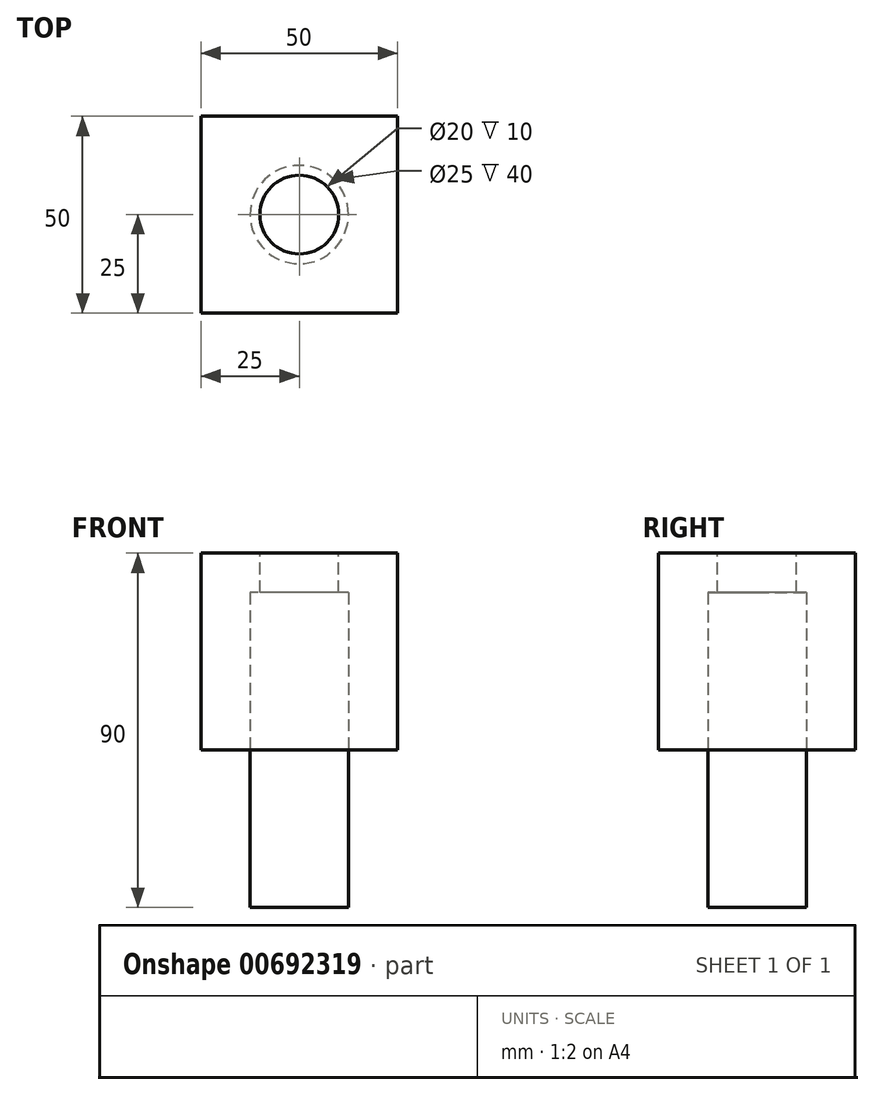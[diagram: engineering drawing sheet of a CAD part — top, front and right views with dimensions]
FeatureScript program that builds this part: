
annotation { "Feature Type Name" : "Feature", "Feature Type Description" : "" }
export const myFeature = defineFeature(function(context is Context, id is Id, definition is map)
    precondition{}
    {
        {
            var Q0;
            Q0=qCreatedBy(makeId("Top.planeOp"),FACE);
            var sketch = newSketch(context, id + "F0", { "sketchPlane" : qUnion([Q0])});
            skLineSegment(sketch, "E0.bottom", {"start": v(25, -25) * mm, "end": v(-25, -25) * mm});
            skLineSegment(sketch, "E0.top", {"start": v(25, 25) * mm, "end": v(-25, 25) * mm});
            skLineSegment(sketch, "E0.left", {"start": v(25, -25) * mm, "end": v(25, 25) * mm});
            skLineSegment(sketch, "E0.right", {"start": v(-25, -25) * mm, "end": v(-25, 25) * mm});
            skPoint(sketch, "E0.middle", {"position": v(0, 0) * mm});
            skSolve(sketch);
        }
        {
            var Q0;
            Q0=makeQuery(id+"F0.imprint","IMPRINT",FACE,{"disambiguationData":[TD([[makeQuery(id+"F0.imprint","IMPRINT",EDGE,{"derivedFrom":sQuery(id+"F0.wireOp",EDGE,"E0.bottom")}),-1.0]])]});
            extrude(context, id + "F1", {"entities" : qUnion([Q0]), "depth" : 50 * mm, "offsetDistance" : 25 * mm});
        }
        {
            var Q0;
            Q0=makeQuery(id+"F1.opExtrude","CAP_FACE",FACE,{"disambiguationData":[OSD([sQuery(id+"F0.wireOp",EDGE,"E0.bottom"),sQuery(id+"F0.wireOp",EDGE,"E0.top"),sQuery(id+"F0.wireOp",EDGE,"E0.left"),sQuery(id+"F0.wireOp",EDGE,"E0.right")])],"isStart":false});
            var sketch = newSketch(context, id + "F2", { "sketchPlane" : qUnion([Q0])});
            skCircle(sketch, "E1", {"center": v(0, 0) * mm, "radius": 10 * mm});
            skSolve(sketch);
        }
        {
            var Q0;
            Q0=makeQuery(id+"F2.imprint","IMPRINT",FACE,{"disambiguationData":[TD([[makeQuery(id+"F2.imprint","IMPRINT",EDGE,{"derivedFrom":sQuery(id+"F2.wireOp",EDGE,"E1")}),1.0]])]});
            extrude(context, id + "F3", {"entities" : qUnion([Q0]), "operationType" : NewBodyOperationType.REMOVE, "oppositeDirection" : true, "depth" : 25 * mm, "offsetDistance" : 25 * mm});
        }
        {
            var Q0;
            Q0=qCreatedBy(makeId("Top.planeOp"),FACE);
            var sketch = newSketch(context, id + "F4", { "sketchPlane" : qUnion([Q0])});
            skCircle(sketch, "E2", {"center": v(0, 0) * mm, "radius": 12.5 * mm});
            skSolve(sketch);
        }
        {
            var Q0;
            Q0=makeQuery(id+"F4.imprint","IMPRINT",FACE,{"disambiguationData":[TD([[makeQuery(id+"F4.imprint","IMPRINT",EDGE,{"derivedFrom":sQuery(id+"F4.wireOp",EDGE,"E2")}),1.0]])]});
            extrude(context, id + "F5", {"entities" : qUnion([Q0]), "endBound" : BoundingType.SYMMETRIC, "depth" : 80 * mm, "offsetDistance" : 25 * mm});
        }
        {
            var Q0;
            Q0=makeQuery(id+"F5.opExtrude","SWEPT_BODY",BODY,{"disambiguationData":[OSD([sQuery(id+"F4.wireOp",EDGE,"E2")])]});
            var Q1;
            Q1=makeQuery(id+"F1.opExtrude","SWEPT_BODY",BODY,{"disambiguationData":[OSD([sQuery(id+"F0.wireOp",EDGE,"E0.bottom"),sQuery(id+"F0.wireOp",EDGE,"E0.top"),sQuery(id+"F0.wireOp",EDGE,"E0.left"),sQuery(id+"F0.wireOp",EDGE,"E0.right")])]});
            booleanBodies(context, id + "F6", {"operationType" : BooleanOperationType.SUBTRACTION, "tools" : qUnion([Q0]), "targets" : qUnion([Q1]), "keepTools" : true});
        }
    });
